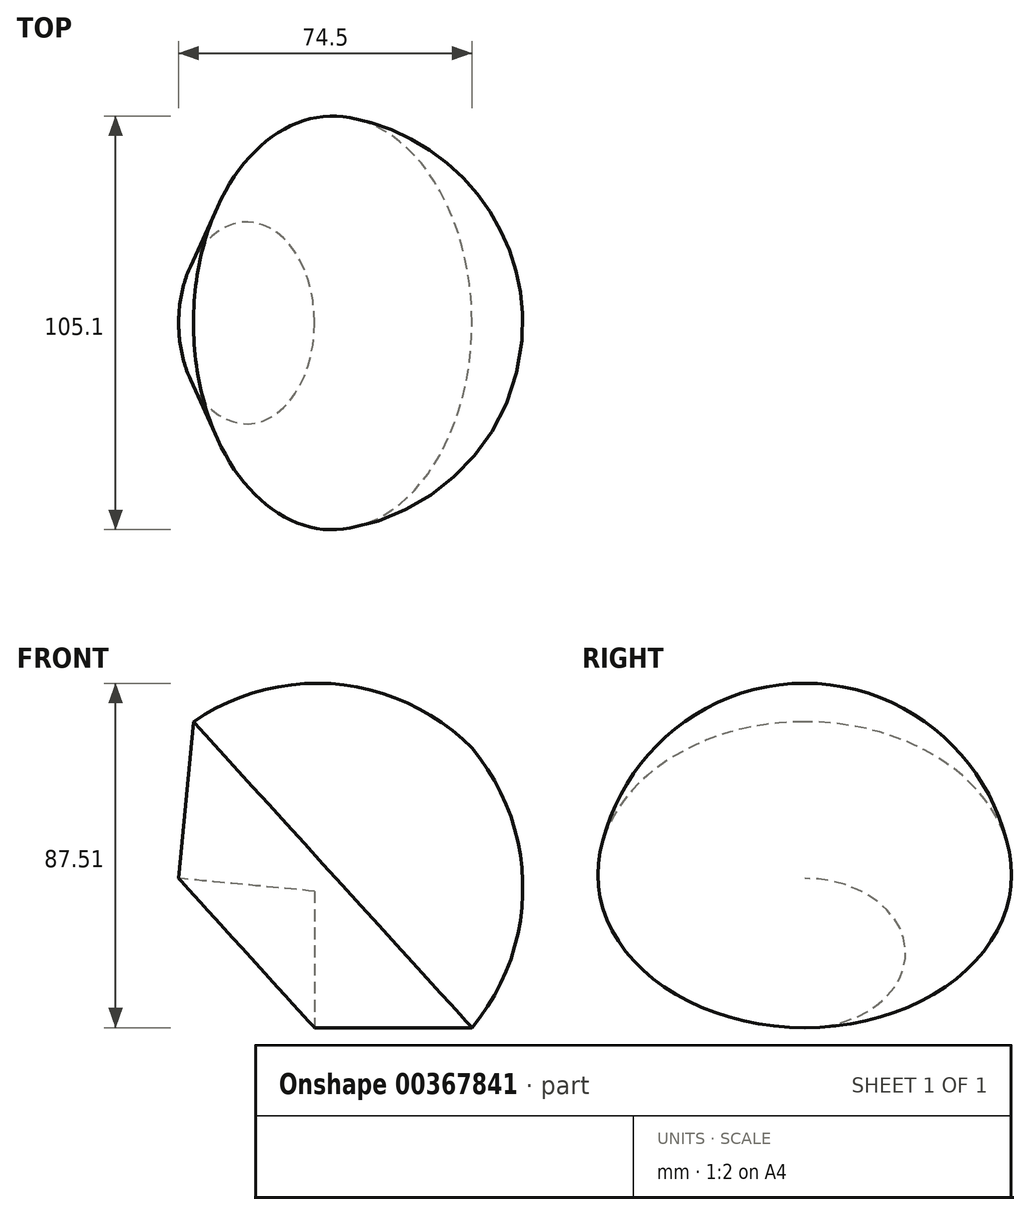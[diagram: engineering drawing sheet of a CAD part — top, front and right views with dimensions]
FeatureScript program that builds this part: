
annotation { "Feature Type Name" : "Feature", "Feature Type Description" : "" }
export const myFeature = defineFeature(function(context is Context, id is Id, definition is map)
    precondition{}
    {
        {
            var Q0;
            Q0=qCreatedBy(makeId("Front.planeOp"),FACE);
            var sketch = newSketch(context, id + "F0", { "sketchPlane" : qUnion([Q0])});
            skLineSegment(sketch, "E0", {"start": v(0, -34.66) * mm, "end": v(40, -34.66) * mm});
            skLineSegment(sketch, "E1", {"start": v(40, 36.4) * mm, "end": v(0, 0) * mm});
            skArc(sketch, "E2", {"start": v(40, -34.66) * mm, "mid": v(52.92, 0.87) * mm, "end": v(40, 36.4) * mm});
            skLineSegment(sketch, "E3", {"start": v(0, 0) * mm, "end": v(0, -34.66) * mm});
            skSolve(sketch);
        }
        {
            var Q0;
            Q0=makeQuery(id+"F0.imprint","IMPRINT",FACE,{"disambiguationData":[TD([[makeQuery(id+"F0.imprint","IMPRINT",EDGE,{"derivedFrom":sQuery(id+"F0.wireOp",EDGE,"E0")}),1.0]])]});
            var Q1;
            Q1=sQuery(id+"F0.wireOp",EDGE,"E1");
            revolve(context, id + "F1", {"entities" : qUnion([Q0]), "axis" : qUnion([Q1]), "revolveType" : RevolveType.FULL});
        }
    });
